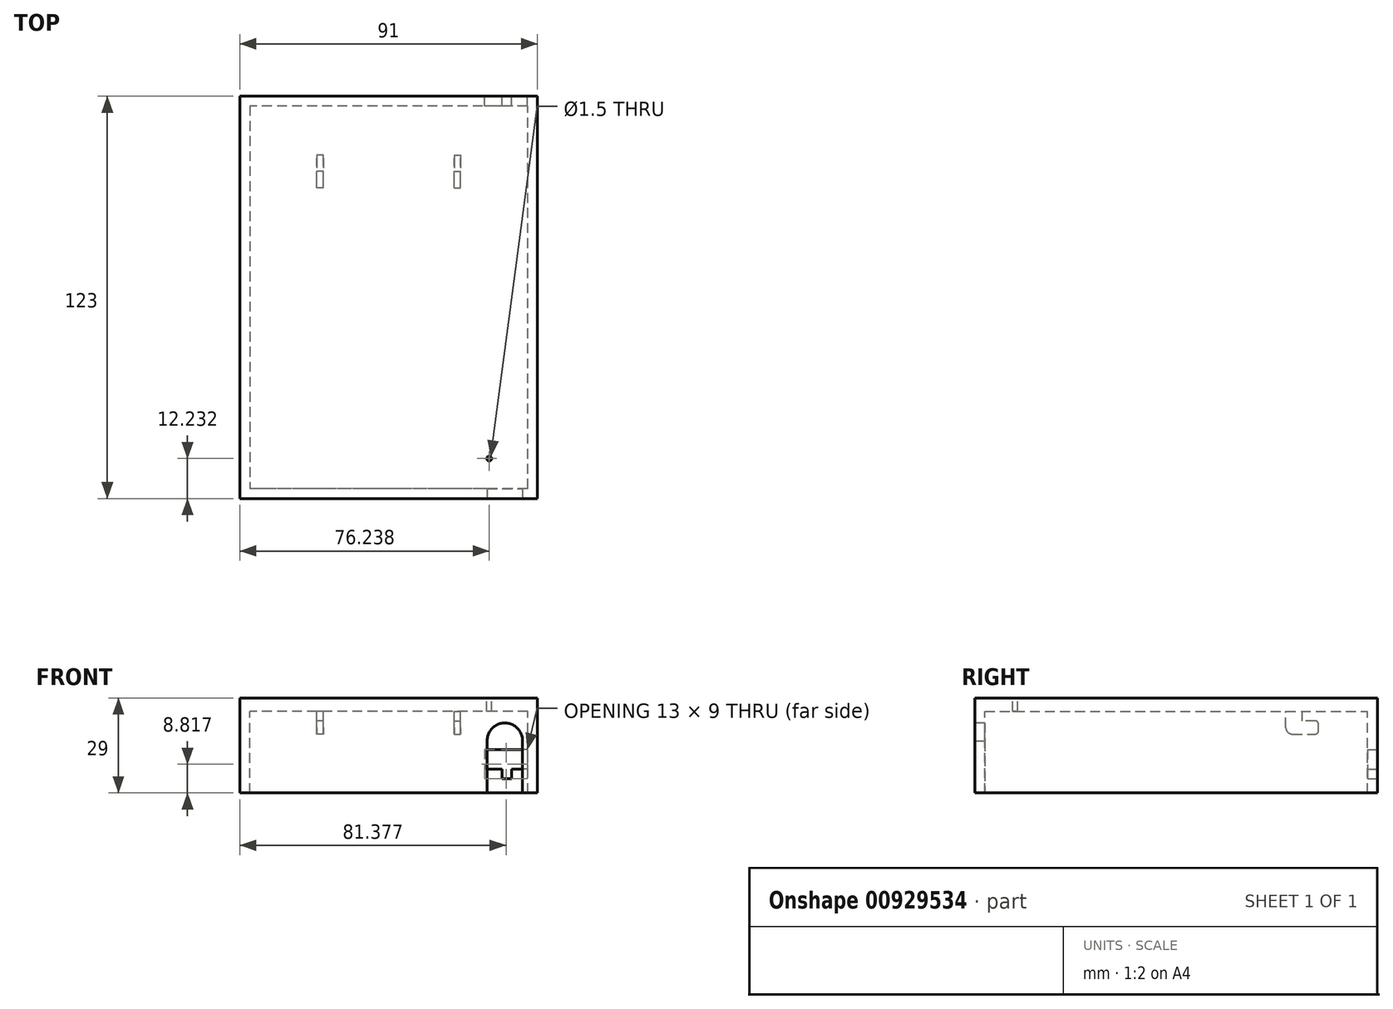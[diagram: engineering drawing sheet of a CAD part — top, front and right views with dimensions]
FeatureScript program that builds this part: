
annotation { "Feature Type Name" : "Feature", "Feature Type Description" : "" }
export const myFeature = defineFeature(function(context is Context, id is Id, definition is map)
    precondition{}
    {
        {
            var Q0;
            Q0=qCreatedBy(makeId("Top.planeOp"),FACE);
            var sketch = newSketch(context, id + "F0", { "sketchPlane" : qUnion([Q0])});
            skLineSegment(sketch, "E0.bottom", {"start": v(42.5, -58.5) * mm, "end": v(-42.5, -58.5) * mm});
            skLineSegment(sketch, "E0.top", {"start": v(42.5, 58.5) * mm, "end": v(-42.5, 58.5) * mm});
            skLineSegment(sketch, "E0.left", {"start": v(42.5, -58.5) * mm, "end": v(42.5, 58.5) * mm});
            skLineSegment(sketch, "E0.right", {"start": v(-42.5, -58.5) * mm, "end": v(-42.5, 58.5) * mm});
            skPoint(sketch, "E0.middle", {"position": v(0, 0) * mm});
            skSolve(sketch);
        }
        {
            var Q0;
            Q0=makeQuery(id+"F0.imprint","IMPRINT",FACE,{"disambiguationData":[TD([[makeQuery(id+"F0.imprint","IMPRINT",EDGE,{"derivedFrom":sQuery(id+"F0.wireOp",EDGE,"E0.bottom")}),-1.0]])]});
            extrude(context, id + "F1", {"entities" : qUnion([Q0]), "depth" : 4 * mm, "offsetDistance" : 25 * mm});
        }
        {
            var Q0;
            Q0=makeQuery(id+"F1.opExtrude","CAP_FACE",FACE,{"disambiguationData":[OSD([sQuery(id+"F0.wireOp",EDGE,"E0.bottom"),sQuery(id+"F0.wireOp",EDGE,"E0.top"),sQuery(id+"F0.wireOp",EDGE,"E0.left"),sQuery(id+"F0.wireOp",EDGE,"E0.right")])],"isStart":true});
            var sketch = newSketch(context, id + "F2", { "sketchPlane" : qUnion([Q0])});
            skLineSegment(sketch, "E1", {"start": v(0, -58.5) * mm, "end": v(0, -33.5) * mm, "construction": true});
            skLineSegment(sketch, "E2", {"start": v(0, -33.5) * mm, "end": v(20, -33.5) * mm, "construction": true});
            skLineSegment(sketch, "E3", {"start": v(0, -33.5) * mm, "end": v(-20, -33.5) * mm, "construction": true});
            skLineSegment(sketch, "E4.bottom", {"start": v(-20, -33.5) * mm, "end": v(-22, -33.5) * mm});
            skLineSegment(sketch, "E4.top", {"start": v(-20, -38.5) * mm, "end": v(-22, -38.5) * mm});
            skLineSegment(sketch, "E4.left", {"start": v(-20, -33.5) * mm, "end": v(-20, -38.5) * mm});
            skLineSegment(sketch, "E4.right", {"start": v(-22, -33.5) * mm, "end": v(-22, -38.5) * mm});
            skSolve(sketch);
        }
        {
            var Q0;
            Q0 = qSketchRegion(id + "F2", true);
            extrude(context, id + "F3", {"entities" : qUnion([Q0]), "operationType" : NewBodyOperationType.ADD, "depth" : 7 * mm, "offsetDistance" : 25 * mm});
        }
        {
            var Q0;
            Q0=makeQuery(id+"F3.opExtrude","SWEPT_FACE",FACE,{"disambiguationData":[OSD([sQuery(id+"F2.wireOp",EDGE,"E4.top")])]});
            var sketch = newSketch(context, id + "F4", { "sketchPlane" : qUnion([Q0])});
            skLineSegment(sketch, "E5.bottom", {"start": v(20, -7) * mm, "end": v(22, -7) * mm});
            skLineSegment(sketch, "E5.top", {"start": v(20, -3) * mm, "end": v(22, -3) * mm});
            skLineSegment(sketch, "E5.left", {"start": v(20, -7) * mm, "end": v(20, -3) * mm});
            skLineSegment(sketch, "E5.right", {"start": v(22, -7) * mm, "end": v(22, -3) * mm});
            skSolve(sketch);
        }
        {
            var Q0;
            Q0 = qSketchRegion(id + "F4", true);
            extrude(context, id + "F5", {"entities" : qUnion([Q0]), "operationType" : NewBodyOperationType.ADD, "depth" : 5 * mm, "offsetDistance" : 25 * mm});
        }
        {
            var Q0;
            Q0=makeQuery(id+"F5.opExtrude","CAP_EDGE",EDGE,{"disambiguationData":[OSD([sQuery(id+"F4.wireOp",EDGE,"E5.top")])],"isStart":false});
            fillet(context, id + "F6", {"entities" : qUnion([Q0]), "radius" : 1 * mm, "tangentPropagation" : true, "allowEdgeOverflow" : false});
        }
        {
            var Q0;
            Q0=makeQuery(id+"F5.opExtrude","CAP_EDGE",EDGE,{"disambiguationData":[OSD([sQuery(id+"F4.wireOp",EDGE,"E5.bottom")])],"isStart":false});
            fillet(context, id + "F7", {"entities" : qUnion([Q0]), "radius" : 1 * mm, "tangentPropagation" : true, "allowEdgeOverflow" : false});
        }
        {
            var Q0;
            Q0=makeQuery(id+"F3.opExtrude","CAP_EDGE",EDGE,{"disambiguationData":[OSD([sQuery(id+"F2.wireOp",EDGE,"E4.bottom")])],"isStart":false});
            fillet(context, id + "F8", {"entities" : qUnion([Q0]), "radius" : 2 * mm, "tangentPropagation" : true, "allowEdgeOverflow" : false});
        }
        {
            var Q0;
            Q0=makeQuery(id+"F1.opExtrude","SWEPT_BODY",BODY,{"disambiguationData":[OSD([sQuery(id+"F0.wireOp",EDGE,"E0.bottom"),sQuery(id+"F0.wireOp",EDGE,"E0.top"),sQuery(id+"F0.wireOp",EDGE,"E0.left"),sQuery(id+"F0.wireOp",EDGE,"E0.right")])]});
            var Q1;
            Q1=qCreatedBy(makeId("Right.planeOp"),FACE);
            mirror(context, id + "F9", {"entities" : qUnion([Q0]), "mirrorPlane" : qUnion([Q1])});
        }
        {
            var Q0;
            Q0=makeQuery(id+"F1.opExtrude","SWEPT_FACE",FACE,{"disambiguationData":[OSD([sQuery(id+"F0.wireOp",EDGE,"E0.left")])]});
            var sketch = newSketch(context, id + "F10", { "sketchPlane" : qUnion([Q0])});
            skSolve(sketch);
        }
        {
            var Q0;
            Q0=makeQuery(id+"F1.opExtrude","SWEPT_FACE",FACE,{"disambiguationData":[OSD([sQuery(id+"F0.wireOp",EDGE,"E0.right")])]});
            var sketch = newSketch(context, id + "F11", { "sketchPlane" : qUnion([Q0])});
            skLineSegment(sketch, "E6.bottom", {"start": v(-58.5, 4) * mm, "end": v(58.5, 4) * mm});
            skLineSegment(sketch, "E6.top", {"start": v(-58.5, 0) * mm, "end": v(58.5, 0) * mm});
            skLineSegment(sketch, "E6.left", {"start": v(-58.5, 4) * mm, "end": v(-58.5, 0) * mm});
            skLineSegment(sketch, "E6.right", {"start": v(58.5, 4) * mm, "end": v(58.5, 0) * mm});
            skSolve(sketch);
        }
        {
            var Q0;
            Q0 = qSketchRegion(id + "F11", true);
            extrude(context, id + "F12", {"entities" : qUnion([Q0]), "operationType" : NewBodyOperationType.ADD, "depth" : 3 * mm, "offsetDistance" : 25 * mm});
        }
        {
            var Q0;
            Q0=makeQuery(id+"F12.boolean.opBoolean","MERGE",FACE,{"derivedFrom":[makeQuery(id+"F1.opExtrude","CAP_FACE",FACE,{"disambiguationData":[OSD([sQuery(id+"F0.wireOp",EDGE,"E0.bottom"),sQuery(id+"F0.wireOp",EDGE,"E0.top"),sQuery(id+"F0.wireOp",EDGE,"E0.left"),sQuery(id+"F0.wireOp",EDGE,"E0.right")])],"isStart":true}),makeQuery(id+"F12.opExtrude","SWEPT_FACE",FACE,{"disambiguationData":[OSD([sQuery(id+"F11.wireOp",EDGE,"E6.top")])]})]});
            var sketch = newSketch(context, id + "F13", { "sketchPlane" : qUnion([Q0])});
            skLineSegment(sketch, "E7.bottom", {"start": v(-45.5, -58.5) * mm, "end": v(-42.5, -58.5) * mm});
            skLineSegment(sketch, "E7.top", {"start": v(-45.5, 58.5) * mm, "end": v(-42.5, 58.5) * mm});
            skLineSegment(sketch, "E7.left", {"start": v(-45.5, -58.5) * mm, "end": v(-45.5, 58.5) * mm});
            skLineSegment(sketch, "E7.right", {"start": v(-42.5, -58.5) * mm, "end": v(-42.5, 58.5) * mm});
            skLineSegment(sketch, "E8.bottom", {"start": v(42.5, 58.5) * mm, "end": v(45.5, 58.5) * mm});
            skLineSegment(sketch, "E8.top", {"start": v(42.5, -58.5) * mm, "end": v(45.5, -58.5) * mm});
            skLineSegment(sketch, "E8.left", {"start": v(42.5, 58.5) * mm, "end": v(42.5, -58.5) * mm});
            skLineSegment(sketch, "E8.right", {"start": v(45.5, 58.5) * mm, "end": v(45.5, -58.5) * mm});
            skLineSegment(sketch, "E9.bottom", {"start": v(-42.5, -58.5) * mm, "end": v(42.5, -58.5) * mm});
            skLineSegment(sketch, "E9.top", {"start": v(-42.5, -61.5) * mm, "end": v(42.5, -61.5) * mm});
            skLineSegment(sketch, "E9.left", {"start": v(-42.5, -58.5) * mm, "end": v(-42.5, -61.5) * mm});
            skLineSegment(sketch, "E9.right", {"start": v(42.5, -58.5) * mm, "end": v(42.5, -61.5) * mm});
            skLineSegment(sketch, "E10.bottom", {"start": v(-42.5, 58.5) * mm, "end": v(42.5, 58.5) * mm});
            skLineSegment(sketch, "E10.top", {"start": v(-42.5, 61.5) * mm, "end": v(42.5, 61.5) * mm});
            skLineSegment(sketch, "E10.left", {"start": v(-42.5, 58.5) * mm, "end": v(-42.5, 61.5) * mm});
            skLineSegment(sketch, "E10.right", {"start": v(42.5, 58.5) * mm, "end": v(42.5, 61.5) * mm});
            skSolve(sketch);
        }
        {
            var Q0;
            {var subQ3=sQuery(id+"F10.wireOp",EDGE,"TnKOkzJ1-PIXF-Fl0i-99ar-zMNN4hUHpWCz");Q0=makeQuery(id+"F10.imprint","IMPRINT",FACE,{"disambiguationData":[TD([[makeQuery(id+"F10.imprint","IMPRINT",EDGE,{"derivedFrom":subQ3}),-1.0]])]});}
            var Q1;
            {var subQ0=sQuery(id+"F0.wireOp",EDGE,"E0.left");Q1=makeQuery(id+"F10.imprint","IMPRINT",FACE,{"disambiguationData":[TD([[makeQuery(id+"F10.imprint","IMPRINT",EDGE,{"derivedFrom":makeQuery(id+"F1.opExtrude","CAP_EDGE",EDGE,{"disambiguationData":[OSD([subQ0])],"isStart":true})}),1.0]])]});}
            extrude(context, id + "F14", {"entities" : qUnion([Q0, Q1]), "operationType" : NewBodyOperationType.ADD, "depth" : 3 * mm, "offsetDistance" : 25 * mm});
        }
        {
            var Q0;
            Q0=makeQuery(id+"F13.imprint","IMPRINT",FACE,{"disambiguationData":[TD([[makeQuery(id+"F13.imprint","IMPRINT",EDGE,{"derivedFrom":sQuery(id+"F13.wireOp",EDGE,"E10.bottom")}),-1.0]])]});
            var Q1;
            Q1=makeQuery(id+"F13.imprint","IMPRINT",FACE,{"disambiguationData":[TD([[makeQuery(id+"F13.imprint","IMPRINT",EDGE,{"derivedFrom":sQuery(id+"F13.wireOp",EDGE,"E9.bottom")}),1.0]])]});
            var Q2;
            Q2=makeQuery(id+"F13.imprint","IMPRINT",FACE,{"disambiguationData":[TD([[makeQuery(id+"F13.imprint","IMPRINT",EDGE,{"derivedFrom":sQuery(id+"F13.wireOp",EDGE,"E7.bottom")}),-1.0]])]});
            var Q3;
            Q3=makeQuery(id+"F13.imprint","IMPRINT",FACE,{"disambiguationData":[TD([[makeQuery(id+"F13.imprint","IMPRINT",EDGE,{"derivedFrom":sQuery(id+"F13.wireOp",EDGE,"E8.bottom")}),-1.0]])]});
            extrude(context, id + "F15", {"entities" : qUnion([Q0, Q1, Q2, Q3]), "operationType" : NewBodyOperationType.ADD, "depth" : 25 * mm, "offsetDistance" : 25 * mm});
        }
        {
            var Q0;
            {var subQ0=sQuery(id+"F0.wireOp",EDGE,"E0.top");Q0=makeQuery(id+"F15.boolean.opBoolean","MERGE",FACE,{"derivedFrom":[makeQuery(id+"F14.boolean.opBoolean","MERGE",FACE,{"derivedFrom":[makeQuery(id+"F12.boolean.opBoolean","MERGE",FACE,{"derivedFrom":[makeQuery(id+"F1.opExtrude","SWEPT_FACE",FACE,{"disambiguationData":[OSD([subQ0])]}),makeQuery(id+"F12.opExtrude","SWEPT_FACE",FACE,{"disambiguationData":[OSD([sQuery(id+"F11.wireOp",EDGE,"E6.left")])]})]}),makeQuery(id+"F14.opExtrude","SWEPT_FACE",FACE,{"disambiguationData":[OSD([subQ0,sQuery(id+"F0.wireOp",EDGE,"E0.left")])]})]}),makeQuery(id+"F15.opExtrude","SWEPT_FACE",FACE,{"disambiguationData":[OSD([sQuery(id+"F13.wireOp",EDGE,"E7.bottom")])]}),makeQuery(id+"F15.opExtrude","SWEPT_FACE",FACE,{"disambiguationData":[OSD([sQuery(id+"F13.wireOp",EDGE,"E8.top")])]})]});}
            extrude(context, id + "F16", {"entities" : qUnion([Q0]), "operationType" : NewBodyOperationType.ADD, "depth" : 3 * mm, "offsetDistance" : 25 * mm});
        }
        {
            var Q0;
            Q0=makeQuery(id+"F16.boolean.opBoolean","MERGE",FACE,{"derivedFrom":[makeQuery(id+"F15.opExtrude","SWEPT_FACE",FACE,{"disambiguationData":[OSD([sQuery(id+"F13.wireOp",EDGE,"E9.top")])]}),makeQuery(id+"F16.opExtrude","CAP_FACE",FACE,{"disambiguationData":[OSD([sQuery(id+"F0.wireOp",EDGE,"E0.top"),sQuery(id+"F0.wireOp",EDGE,"E0.left"),sQuery(id+"F11.wireOp",EDGE,"E6.left"),sQuery(id+"F13.wireOp",EDGE,"E7.bottom"),sQuery(id+"F13.wireOp",EDGE,"E8.top")])],"isStart":false})]});
            var sketch = newSketch(context, id + "F17", { "sketchPlane" : qUnion([Q0])});
            skLineSegment(sketch, "E11.bottom", {"start": v(-42.38, -11.68) * mm, "end": v(-29.38, -11.68) * mm});
            skLineSegment(sketch, "E11.top", {"start": v(-42.38, -17.68) * mm, "end": v(-37.63, -17.68) * mm});
            skLineSegment(sketch, "E11.left", {"start": v(-42.38, -11.68) * mm, "end": v(-42.38, -17.68) * mm});
            skLineSegment(sketch, "E11.right", {"start": v(-29.38, -11.68) * mm, "end": v(-29.38, -17.68) * mm});
            skLineSegment(sketch, "E12.top", {"start": v(-37.63, -20.68) * mm, "end": v(-34.63, -20.68) * mm});
            skLineSegment(sketch, "E12.left", {"start": v(-37.63, -17.68) * mm, "end": v(-37.63, -20.68) * mm});
            skLineSegment(sketch, "E12.right", {"start": v(-34.63, -17.68) * mm, "end": v(-34.63, -20.68) * mm});
            skLineSegment(sketch, "E13.trimOffspring", {"start": v(-34.63, -17.68) * mm, "end": v(-29.38, -17.68) * mm});
            skSolve(sketch);
        }
        {
            var Q0;
            Q0=makeQuery(id+"F17.imprint","IMPRINT",FACE,{"disambiguationData":[TD([[makeQuery(id+"F17.imprint","IMPRINT",EDGE,{"derivedFrom":sQuery(id+"F17.wireOp",EDGE,"E11.bottom")}),-1.0]])]});
            extrude(context, id + "F18", {"entities" : qUnion([Q0]), "operationType" : NewBodyOperationType.REMOVE, "oppositeDirection" : true, "depth" : 3 * mm, "offsetDistance" : 25 * mm});
        }
        {
            var Q0;
            {var subQ0=sQuery(id+"F11.wireOp",EDGE,"E6.bottom");var subQ1=sQuery(id+"F0.wireOp",EDGE,"E0.left");var subQ2=sQuery(id+"F0.wireOp",EDGE,"E0.top");Q0=makeQuery(id+"F16.boolean.opBoolean","MERGE",FACE,{"derivedFrom":[makeQuery(id+"F14.boolean.opBoolean","MERGE",FACE,{"derivedFrom":[makeQuery(id+"F12.boolean.opBoolean","MERGE",FACE,{"derivedFrom":[makeQuery(id+"F1.opExtrude","CAP_FACE",FACE,{"disambiguationData":[OSD([sQuery(id+"F0.wireOp",EDGE,"E0.bottom"),subQ2,subQ1,sQuery(id+"F0.wireOp",EDGE,"E0.right")])],"isStart":false}),makeQuery(id+"F12.opExtrude","SWEPT_FACE",FACE,{"disambiguationData":[OSD([subQ0])]})]}),makeQuery(id+"F14.opExtrude","SWEPT_FACE",FACE,{"disambiguationData":[OSD([subQ1]),TDD([makeQuery(id+"F10.imprint","IMPRINT",EDGE,{"derivedFrom":makeQuery(id+"F1.opExtrude","CAP_EDGE",EDGE,{"disambiguationData":[OSD([subQ1])],"isStart":false})})])]})]}),makeQuery(id+"F16.opExtrude","SWEPT_FACE",FACE,{"disambiguationData":[OSD([subQ2,subQ1,subQ0,sQuery(id+"F11.wireOp",EDGE,"E6.left")])]})]});}
            var sketch = newSketch(context, id + "F19", { "sketchPlane" : qUnion([Q0])});
            skCircle(sketch, "E14", {"center": v(30.74, -49.27) * mm, "radius": 0.75 * mm});
            skSolve(sketch);
        }
        {
            var Q0;
            Q0=makeQuery(id+"F19.imprint","IMPRINT",FACE,{"disambiguationData":[TD([[makeQuery(id+"F19.imprint","IMPRINT",EDGE,{"derivedFrom":sQuery(id+"F19.wireOp",EDGE,"E14")}),1.0]])]});
            extrude(context, id + "F20", {"entities" : qUnion([Q0]), "operationType" : NewBodyOperationType.REMOVE, "endBound" : BoundingType.UP_TO_NEXT, "oppositeDirection" : true, "depth" : 25 * mm, "offsetDistance" : 25 * mm});
        }
        {
            var Q0;
            {var subQ0=sQuery(id+"F0.wireOp",EDGE,"E0.bottom");Q0=makeQuery(id+"F15.boolean.opBoolean","MERGE",FACE,{"derivedFrom":[makeQuery(id+"F14.boolean.opBoolean","MERGE",FACE,{"derivedFrom":[makeQuery(id+"F12.boolean.opBoolean","MERGE",FACE,{"derivedFrom":[makeQuery(id+"F1.opExtrude","SWEPT_FACE",FACE,{"disambiguationData":[OSD([subQ0])]}),makeQuery(id+"F12.opExtrude","SWEPT_FACE",FACE,{"disambiguationData":[OSD([sQuery(id+"F11.wireOp",EDGE,"E6.right")])]})]}),makeQuery(id+"F14.opExtrude","SWEPT_FACE",FACE,{"disambiguationData":[OSD([subQ0,sQuery(id+"F0.wireOp",EDGE,"E0.left")])]})]}),makeQuery(id+"F15.opExtrude","SWEPT_FACE",FACE,{"disambiguationData":[OSD([sQuery(id+"F13.wireOp",EDGE,"E7.top")])]}),makeQuery(id+"F15.opExtrude","SWEPT_FACE",FACE,{"disambiguationData":[OSD([sQuery(id+"F13.wireOp",EDGE,"E8.bottom")])]})]});}
            extrude(context, id + "F21", {"entities" : qUnion([Q0]), "operationType" : NewBodyOperationType.ADD, "depth" : 3 * mm, "offsetDistance" : 25 * mm});
        }
        {
            var Q0;
            Q0=makeQuery(id+"F21.boolean.opBoolean","MERGE",FACE,{"derivedFrom":[makeQuery(id+"F15.opExtrude","SWEPT_FACE",FACE,{"disambiguationData":[OSD([sQuery(id+"F13.wireOp",EDGE,"E10.top")])]}),makeQuery(id+"F21.opExtrude","CAP_FACE",FACE,{"disambiguationData":[OSD([sQuery(id+"F0.wireOp",EDGE,"E0.bottom"),sQuery(id+"F0.wireOp",EDGE,"E0.left"),sQuery(id+"F11.wireOp",EDGE,"E6.right"),sQuery(id+"F13.wireOp",EDGE,"E7.top"),sQuery(id+"F13.wireOp",EDGE,"E8.bottom")])],"isStart":false})]});
            var sketch = newSketch(context, id + "F22", { "sketchPlane" : qUnion([Q0])});
            skArc(sketch, "E15", {"start": v(40.91, -9.16) * mm, "mid": v(35.47, -3.6) * mm, "end": v(30.12, -9.25) * mm});
            skLineSegment(sketch, "E16", {"start": v(30.12, -9.25) * mm, "end": v(30.12, -25) * mm});
            skLineSegment(sketch, "E17", {"start": v(40.91, -9.16) * mm, "end": v(40.91, -25) * mm});
            skLineSegment(sketch, "E18", {"start": v(30.12, -25) * mm, "end": v(40.91, -25) * mm});
            skSolve(sketch);
        }
        {
            var Q0;
            Q0=makeQuery(id+"F22.imprint","IMPRINT",FACE,{"disambiguationData":[TD([[makeQuery(id+"F22.imprint","IMPRINT",EDGE,{"derivedFrom":sQuery(id+"F22.wireOp",EDGE,"E15")}),1.0]])]});
            extrude(context, id + "F23", {"entities" : qUnion([Q0]), "operationType" : NewBodyOperationType.REMOVE, "endBound" : BoundingType.UP_TO_NEXT, "oppositeDirection" : true, "depth" : 25 * mm, "offsetDistance" : 25 * mm});
        }
    });
